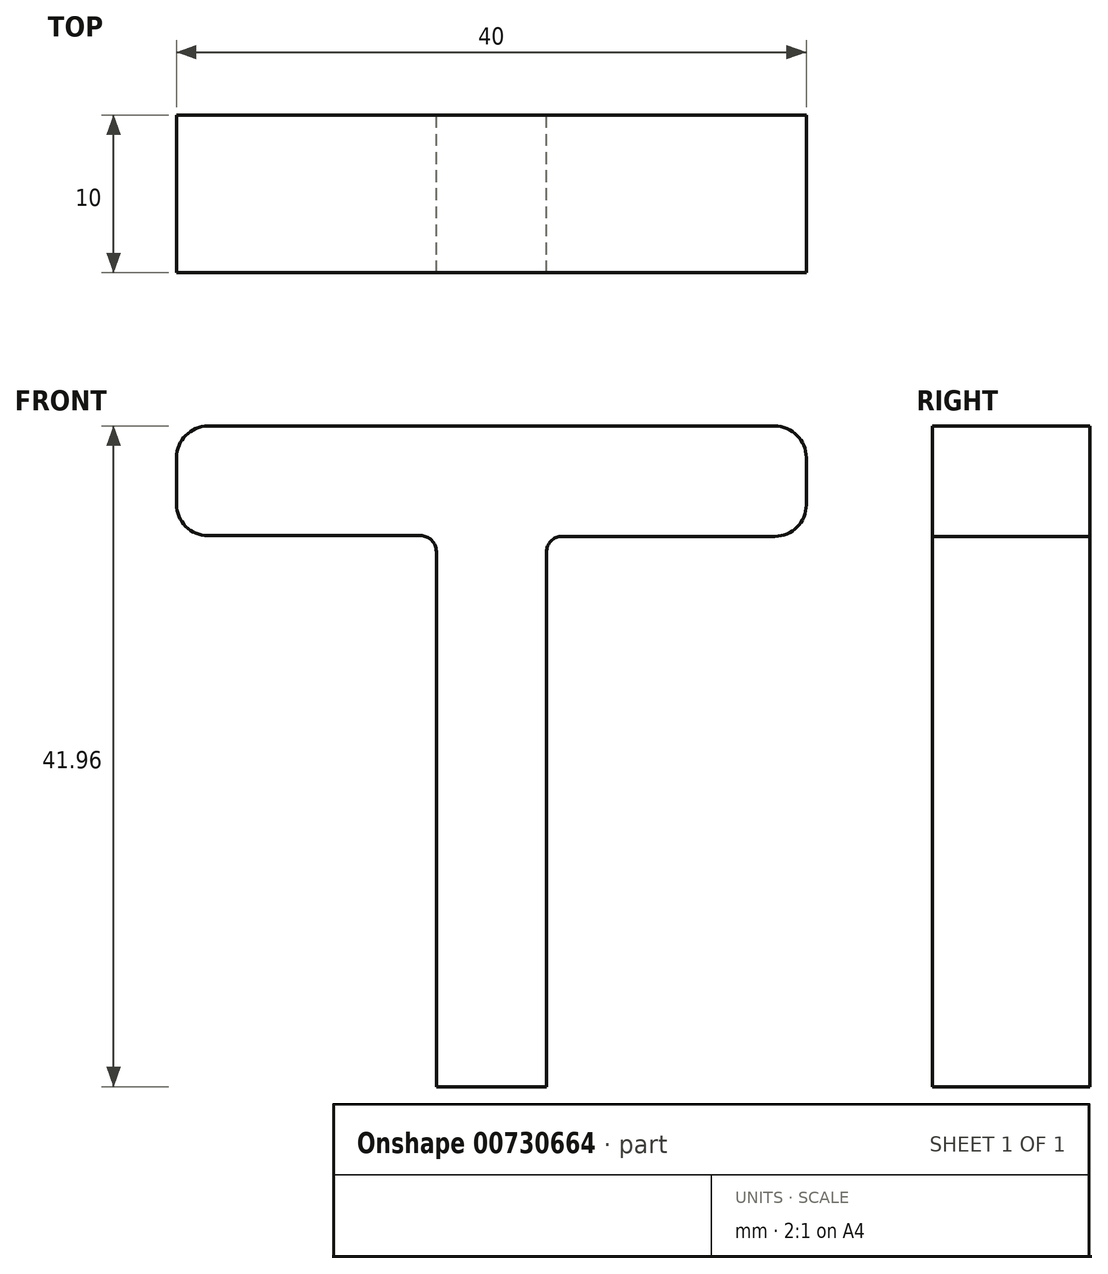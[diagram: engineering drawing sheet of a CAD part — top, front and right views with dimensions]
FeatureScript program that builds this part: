
annotation { "Feature Type Name" : "Feature", "Feature Type Description" : "" }
export const myFeature = defineFeature(function(context is Context, id is Id, definition is map)
    precondition{}
    {
        {
            var Q0;
            Q0=qCreatedBy(makeId("Front.planeOp"),FACE);
            var sketch = newSketch(context, id + "F0", { "sketchPlane" : qUnion([Q0])});
            skLineSegment(sketch, "E0", {"start": v(0, -18.82) * mm, "end": v(0, 16.18) * mm});
            skLineSegment(sketch, "E1", {"start": v(0, 16.18) * mm, "end": v(-5, 16.18) * mm});
            skLineSegment(sketch, "E2", {"start": v(23.5, 16.14) * mm, "end": v(23.5, 23.14) * mm});
            skLineSegment(sketch, "E3", {"start": v(23.5, 23.14) * mm, "end": v(-16.5, 23.14) * mm});
            skLineSegment(sketch, "E4", {"start": v(-16.5, 23.14) * mm, "end": v(-16.5, 16.18) * mm});
            skLineSegment(sketch, "E5", {"start": v(-16.5, 16.18) * mm, "end": v(-5, 16.18) * mm});
            skLineSegment(sketch, "E6", {"start": v(23.5, 16.14) * mm, "end": v(7, 16.14) * mm});
            skLineSegment(sketch, "E7", {"start": v(7, 16.14) * mm, "end": v(7, -18.82) * mm});
            skLineSegment(sketch, "E8", {"start": v(7, -18.82) * mm, "end": v(0, -18.82) * mm});
            skSolve(sketch);
        }
        {
            var Q0;
            Q0=qSketchRegion(id+"F0",true);
            extrude(context, id + "F1", {"entities" : qUnion([Q0]), "depth" : 10 * mm, "offsetDistance" : 25 * mm});
        }
        {
            var Q0;
            Q0=makeQuery(id+"F1.opExtrude","SWEPT_EDGE",EDGE,{"disambiguationData":[OSD([sQuery(id+"F0.wireOp",EDGE,"E3"),sQuery(id+"F0.wireOp",EDGE,"E4")])]});
            var Q1;
            Q1=makeQuery(id+"F1.opExtrude","SWEPT_EDGE",EDGE,{"disambiguationData":[OSD([sQuery(id+"F0.wireOp",EDGE,"E2"),sQuery(id+"F0.wireOp",EDGE,"E3")])]});
            var Q2;
            Q2=makeQuery(id+"F1.opExtrude","SWEPT_EDGE",EDGE,{"disambiguationData":[OSD([sQuery(id+"F0.wireOp",EDGE,"E4"),sQuery(id+"F0.wireOp",EDGE,"E5")])]});
            var Q3;
            Q3=makeQuery(id+"F1.opExtrude","SWEPT_EDGE",EDGE,{"disambiguationData":[OSD([sQuery(id+"F0.wireOp",EDGE,"E2"),sQuery(id+"F0.wireOp",EDGE,"E6")])]});
            fillet(context, id + "F2", {"entities" : qUnion([Q0, Q1, Q2, Q3]), "radius" : 2 * mm, "tangentPropagation" : true, "allowEdgeOverflow" : false});
        }
        {
            var Q0;
            Q0=makeQuery(id+"F1.opExtrude","SWEPT_EDGE",EDGE,{"disambiguationData":[OSD([sQuery(id+"F0.wireOp",EDGE,"E0"),sQuery(id+"F0.wireOp",EDGE,"E1")])]});
            var Q1;
            Q1=makeQuery(id+"F1.opExtrude","SWEPT_EDGE",EDGE,{"disambiguationData":[OSD([sQuery(id+"F0.wireOp",EDGE,"E6"),sQuery(id+"F0.wireOp",EDGE,"E7")])]});
            fillet(context, id + "F3", {"entities" : qUnion([Q0, Q1]), "radius" : 1 * mm, "tangentPropagation" : true, "allowEdgeOverflow" : false});
        }
    });
